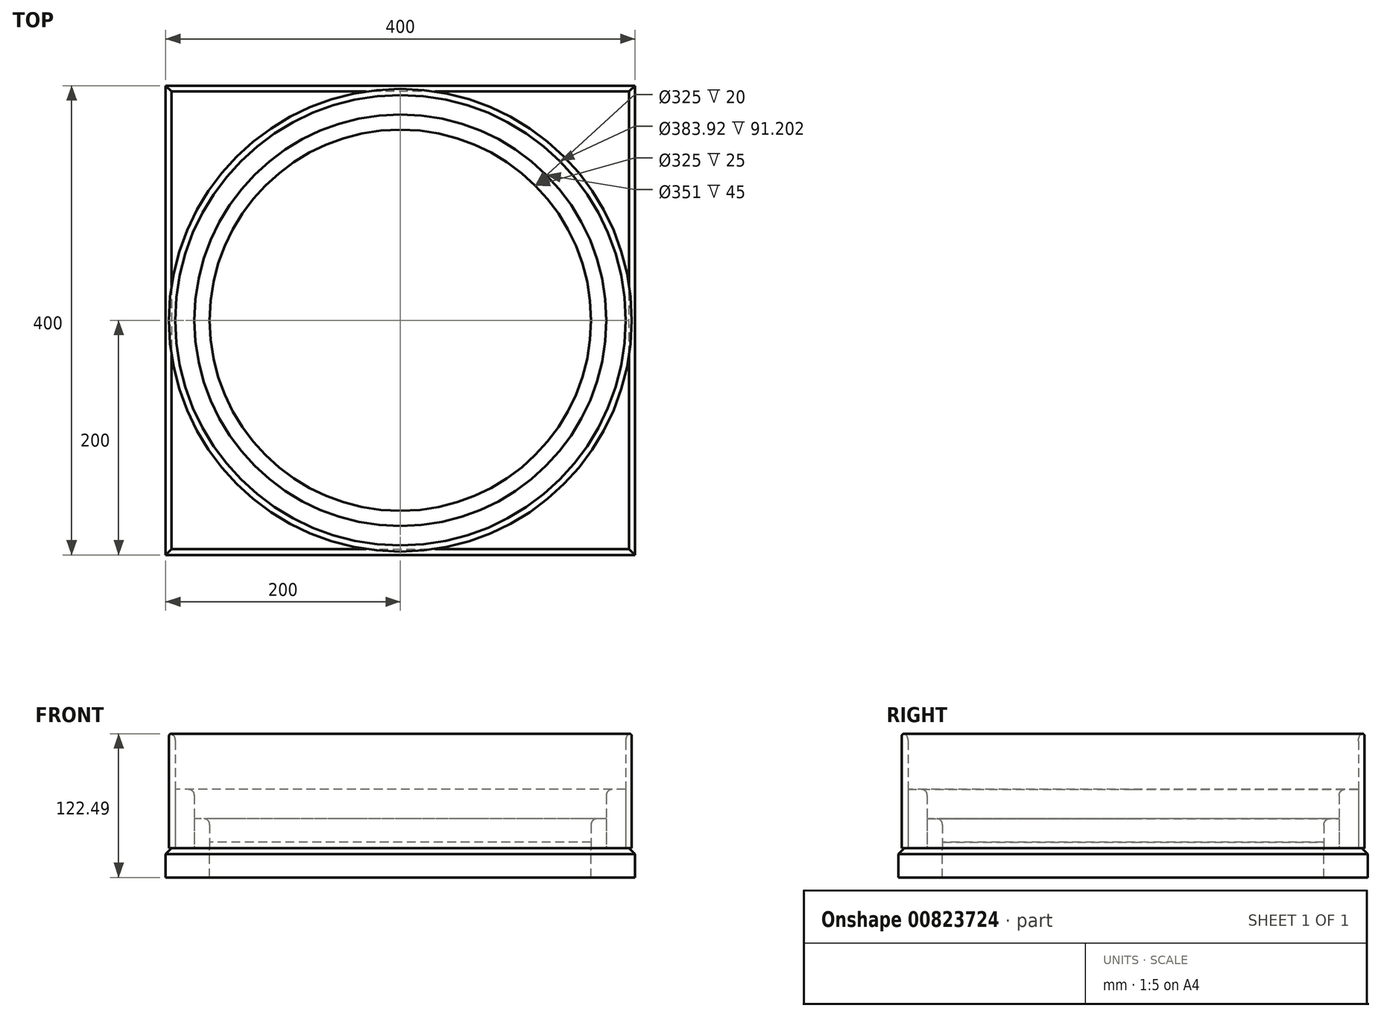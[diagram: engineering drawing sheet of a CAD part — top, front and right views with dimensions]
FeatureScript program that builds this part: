
annotation { "Feature Type Name" : "Feature", "Feature Type Description" : "" }
export const myFeature = defineFeature(function(context is Context, id is Id, definition is map)
    precondition{}
    {
        {
            var Q0;
            Q0=qCreatedBy(makeId("Top.planeOp"),FACE);
            var sketch = newSketch(context, id + "F0", { "sketchPlane" : qUnion([Q0])});
            skCircle(sketch, "E0", {"center": v(0, 0) * mm, "radius": 197.2 * mm});
            skCircle(sketch, "E1", {"center": v(0, 0) * mm, "radius": 175.5 * mm});
            skCircle(sketch, "E2", {"center": v(0, 0) * mm, "radius": 162.5 * mm});
            skCircle(sketch, "E3", {"center": v(0, 0) * mm, "radius": 191.96 * mm});
            skSolve(sketch);
        }
        {
            var Q0;
            Q0=sQuery(id+"F0.wireOp",EDGE,"E0");
            extrude(context, id + "F1", {"bodyType" : ToolBodyType.SURFACE, "surfaceEntities" : qUnion([Q0]), "depth" : 50 * mm, "offsetDistance" : 25 * mm});
        }
        {
            var Q0;
            Q0=makeQuery(id+"F0.imprint","IMPRINT",FACE,{"disambiguationData":[TD([[makeQuery(id+"F0.imprint","IMPRINT",EDGE,{"derivedFrom":sQuery(id+"F0.wireOp",EDGE,"E0")}),1.0]])]});
            extrude(context, id + "F2", {"entities" : qUnion([Q0]), "depth" : 100 * mm, "offsetDistance" : 25 * mm});
        }
        {
            var Q0;
            Q0=sQuery(id+"F0.wireOp",EDGE,"E2");
            extrude(context, id + "F3", {"bodyType" : ToolBodyType.SURFACE, "surfaceEntities" : qUnion([Q0]), "depth" : 5 * mm, "offsetDistance" : 25 * mm});
        }
        {
            var Q0;
            Q0=sQuery(id+"F0.wireOp",EDGE,"E1");
            extrude(context, id + "F4", {"bodyType" : ToolBodyType.SURFACE, "surfaceEntities" : qUnion([Q0]), "depth" : 25 * mm, "offsetDistance" : 25 * mm});
        }
        {
            var Q0;
            Q0=makeQuery(id+"F0.imprint","IMPRINT",FACE,{"disambiguationData":[TD([[makeQuery(id+"F0.imprint","IMPRINT",EDGE,{"derivedFrom":sQuery(id+"F0.wireOp",EDGE,"E2")}),1.0]])]});
            extrude(context, id + "F5", {"entities" : qUnion([Q0]), "depth" : 5 * mm, "offsetDistance" : 25 * mm});
        }
        {
            var Q0;
            Q0=makeQuery(id+"F0.imprint","IMPRINT",FACE,{"disambiguationData":[TD([[makeQuery(id+"F0.imprint","IMPRINT",EDGE,{"derivedFrom":sQuery(id+"F0.wireOp",EDGE,"E1")}),1.0]])]});
            extrude(context, id + "F6", {"entities" : qUnion([Q0]), "depth" : 25 * mm, "offsetDistance" : 25 * mm});
        }
        {
            var Q0;
            Q0=makeQuery(id+"F6.opExtrude","CAP_EDGE",EDGE,{"disambiguationData":[OSD([sQuery(id+"F0.wireOp",EDGE,"E2")])],"isStart":false});
            fillet(context, id + "F7", {"entities" : qUnion([Q0]), "radius" : 5 * mm, "tangentPropagation" : true, "allowEdgeOverflow" : false});
        }
        {
            var Q0;
            Q0=sQuery(id+"F0.wireOp",EDGE,"E3");
            extrude(context, id + "F8", {"bodyType" : ToolBodyType.SURFACE, "surfaceEntities" : qUnion([Q0]), "depth" : 10 * mm, "offsetDistance" : 25 * mm});
        }
        {
            var Q0;
            Q0=makeQuery(id+"F0.imprint","IMPRINT",FACE,{"disambiguationData":[TD([[makeQuery(id+"F0.imprint","IMPRINT",EDGE,{"derivedFrom":sQuery(id+"F0.wireOp",EDGE,"E1")}),-1.0]])]});
            extrude(context, id + "F9", {"entities" : qUnion([Q0]), "depth" : 50 * mm, "offsetDistance" : 25 * mm});
        }
        {
            var Q0;
            Q0=makeQuery(id+"F9.opExtrude","CAP_EDGE",EDGE,{"disambiguationData":[OSD([sQuery(id+"F0.wireOp",EDGE,"E1")])],"isStart":false});
            fillet(context, id + "F10", {"entities" : qUnion([Q0]), "radius" : 5 * mm, "tangentPropagation" : true, "allowEdgeOverflow" : false});
        }
        {
            var Q0;
            Q0=makeQuery(id+"F2.opExtrude","CAP_EDGE",EDGE,{"disambiguationData":[OSD([sQuery(id+"F0.wireOp",EDGE,"E3")])],"isStart":false});
            fillet(context, id + "F11", {"entities" : qUnion([Q0]), "radius" : 10 * mm, "tangentPropagation" : true, "allowEdgeOverflow" : false});
        }
        {
            var Q0;
            Q0=makeQuery(id+"F11.opFillet","BLEND_EDGE",EDGE,{"blendedFrom":[makeQuery(id+"F2.opExtrude","CAP_EDGE",EDGE,{"disambiguationData":[OSD([sQuery(id+"F0.wireOp",EDGE,"E3")])],"isStart":false}),makeQuery(id+"F2.opExtrude","SWEPT_FACE",FACE,{"disambiguationData":[OSD([sQuery(id+"F0.wireOp",EDGE,"E0")])]})],"blendedInto":[makeQuery(id+"F2.opExtrude","SWEPT_FACE",FACE,{"disambiguationData":[OSD([sQuery(id+"F0.wireOp",EDGE,"E0")])]})]});
            fillet(context, id + "F12", {"entities" : qUnion([Q0]), "radius" : 2 * mm, "tangentPropagation" : true, "allowEdgeOverflow" : false});
        }
        {
            var Q0;
            Q0=makeQuery(id+"F5.opExtrude","CAP_FACE",FACE,{"disambiguationData":[OSD([sQuery(id+"F0.wireOp",EDGE,"E2")])],"isStart":true});
            var sketch = newSketch(context, id + "F13", { "sketchPlane" : qUnion([Q0])});
            skLineSegment(sketch, "E4.bottom", {"start": v(-200, -200) * mm, "end": v(200, -200) * mm});
            skLineSegment(sketch, "E4.top", {"start": v(-200, 200) * mm, "end": v(200, 200) * mm});
            skLineSegment(sketch, "E4.left", {"start": v(-200, -200) * mm, "end": v(-200, 200) * mm});
            skLineSegment(sketch, "E4.right", {"start": v(200, -200) * mm, "end": v(200, 200) * mm});
            skPoint(sketch, "E4.middle", {"position": v(0, 0) * mm});
            skSolve(sketch);
        }
        {
            var Q0;
            Q0=makeQuery(id+"F13.imprint","IMPRINT",FACE,{"disambiguationData":[TD([[makeQuery(id+"F13.imprint","IMPRINT",EDGE,{"derivedFrom":sQuery(id+"F13.wireOp",EDGE,"E4.bottom")}),1.0]])]});
            extrude(context, id + "F14", {"entities" : qUnion([Q0]), "depth" : 25 * mm, "offsetDistance" : 25 * mm});
        }
        {
            var Q0;
            Q0=makeQuery(id+"F13.imprint","IMPRINT",FACE,{"disambiguationData":[TD([[makeQuery(id+"F13.imprint","IMPRINT",EDGE,{"derivedFrom":makeQuery(id+"F5.opExtrude","CAP_EDGE",EDGE,{"disambiguationData":[OSD([sQuery(id+"F0.wireOp",EDGE,"E2")])],"isStart":true})}),-1.0]])]});
            extrude(context, id + "F15", {"entities" : qUnion([Q0]), "depth" : 25 * mm, "offsetDistance" : 25 * mm});
        }
        {
            var Q0;
            Q0=makeQuery(id+"F14.opExtrude","CAP_EDGE",EDGE,{"disambiguationData":[OSD([sQuery(id+"F13.wireOp",EDGE,"E4.top")])],"isStart":true});
            chamfer(context, id + "F16", {"entities" : qUnion([Q0]), "width" : 5 * mm, "tangentPropagation" : true});
        }
        {
            var Q0;
            Q0=makeQuery(id+"F14.opExtrude","CAP_EDGE",EDGE,{"disambiguationData":[OSD([sQuery(id+"F13.wireOp",EDGE,"E4.right")])],"isStart":true});
            chamfer(context, id + "F17", {"entities" : qUnion([Q0]), "width" : 5 * mm, "tangentPropagation" : true});
        }
        {
            var Q0;
            Q0=makeQuery(id+"F14.opExtrude","CAP_EDGE",EDGE,{"disambiguationData":[OSD([sQuery(id+"F13.wireOp",EDGE,"E4.bottom")])],"isStart":true});
            chamfer(context, id + "F18", {"entities" : qUnion([Q0]), "width" : 5 * mm, "tangentPropagation" : true});
        }
        {
            var Q0;
            Q0=makeQuery(id+"F14.opExtrude","CAP_EDGE",EDGE,{"disambiguationData":[OSD([sQuery(id+"F13.wireOp",EDGE,"E4.left")])],"isStart":true});
            chamfer(context, id + "F19", {"entities" : qUnion([Q0]), "width" : 5 * mm, "tangentPropagation" : true});
        }
    });
